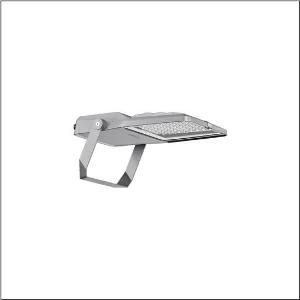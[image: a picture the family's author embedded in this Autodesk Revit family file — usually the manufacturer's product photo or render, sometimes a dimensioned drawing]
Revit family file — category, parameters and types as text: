
# Revit family: floodlight_fl_21_iq_mini___pl64_5xa7772b5e1a_cdb2
name_source: partatom
category: Lighting Fixtures
units: mm (PartAtom-declared; Revit-internal decimal feet)

## family parameters
Cut with Voids When Loaded = No
Host = Face
Light Source = No
Part Type = Normal
Room Calculation Point = No
Round Connector Dimension = Use Diameter
Shared = No

## types (1)
- --- (1 x LED, 5620 lm, 45.5 W, 4000K)
    Apparent Load = 46 VA
    CIE Flux Codes = 28 80 98 100 100
    Color Rendering = 80
    Color Temperature = 4000K
    Default Elevation = 1800 mm
    Description = Floodlight FL 21 iQ mini, floodlight, primary light control with lens, of PMMA, primary optical cover: protective disc, of toughened safety glass, transparent, light distribution: PL64, light emission: direct distribution, installation type: surface-mounted, LED, High Power LED, rated luminous flux: 5.620lm, luminous efficacy: 124lm/W, light colour: 840, colour temperature: 4000K, control: Street-Remote, Auto-Match, Temp-Guard, Night-Set, Smart-Wire, Desk-Remote (wireless, voltage-free reading and setting of iQ features in the workshop via application-optimized NFC function/RFID function), optimised constant luminous flux control (CLO 2.0), with terminal, 6-pole, mains connection: 220..240V, AC, 50/60Hz, start of lifetime: 46W, end of service life: 48W, reduction: 22W, luminaire housing, of diecast aluminium, powder-coated, Siteco® metallic grey (DB 702S), corrosivity category C5 mid according to DIN EN ISO 12944, sealing non-destructively replaceable, mounting bracket, of steel, galvanised, powder-coated, Siteco® metallic grey (DB 702S), protection rating (complete): IP66, insulation class (complete): insulation class II (safety insulation), certification: CE, ENEC, VDE, protection symbol: D, impact resistance: IK08, permissible operating ambient temperature: -40..+40°C, permissible operating ambient temperature for outdoor applications: -40..+50°C, standard: DIN EN 12944, LABS conformity tested according to VDMA 24364:2018-05, packaging unit: 1 piece

Light Distribution: PL64
    Height = 70 mm
    Lamp = 1 x LED
    Lamp Light Flux = 5620 lm
    Lamp Power = 45.5 W
    Lamp count = 1
    Length = 485 mm
    Luminous efficacy = 124 lm/W
    Manufacturer = Siteco
    ModVariant = No
    Model = 5XA7772B5E1A
    Number of Poles = 1
    OnlyDefault = Yes
    Power Factor = 1
    Product Name = Floodlight FL 21 iQ mini | PL64
    Product group = floodlight | pylon annexe
    ProductGroupID = 6200
    Protection Class = Protection class II
    Protection Degree = IP 66
    RLX_Detail_Level = 1
    RLX_Emergency_Light_Flux = 0 lm
    RLX_Emergency_Type = 0
    RLX_Emergency_Type_DB = No
    RlxData = <blob elided: 96033 chars, md5=0f0584d4>
    Socket = socket
    Standby Power = 0 W
    System Light Flux = 5620 lm
    System Power = 46 W
    Type Comments = factory setting: luminous flux: 100 % | dim-lin: 254 | 463 mA
    Type Image = l_1006845.jpg
    URL = http://relux.com
    VarID = @adj_116873
    Voltage = 0 V
    Weight = 0.00 kg
    Width = 337 mm

## geometry (parser evidence)
native form markers: Blend x4, Sweep x11
no freeform markers — native parametric forms only
